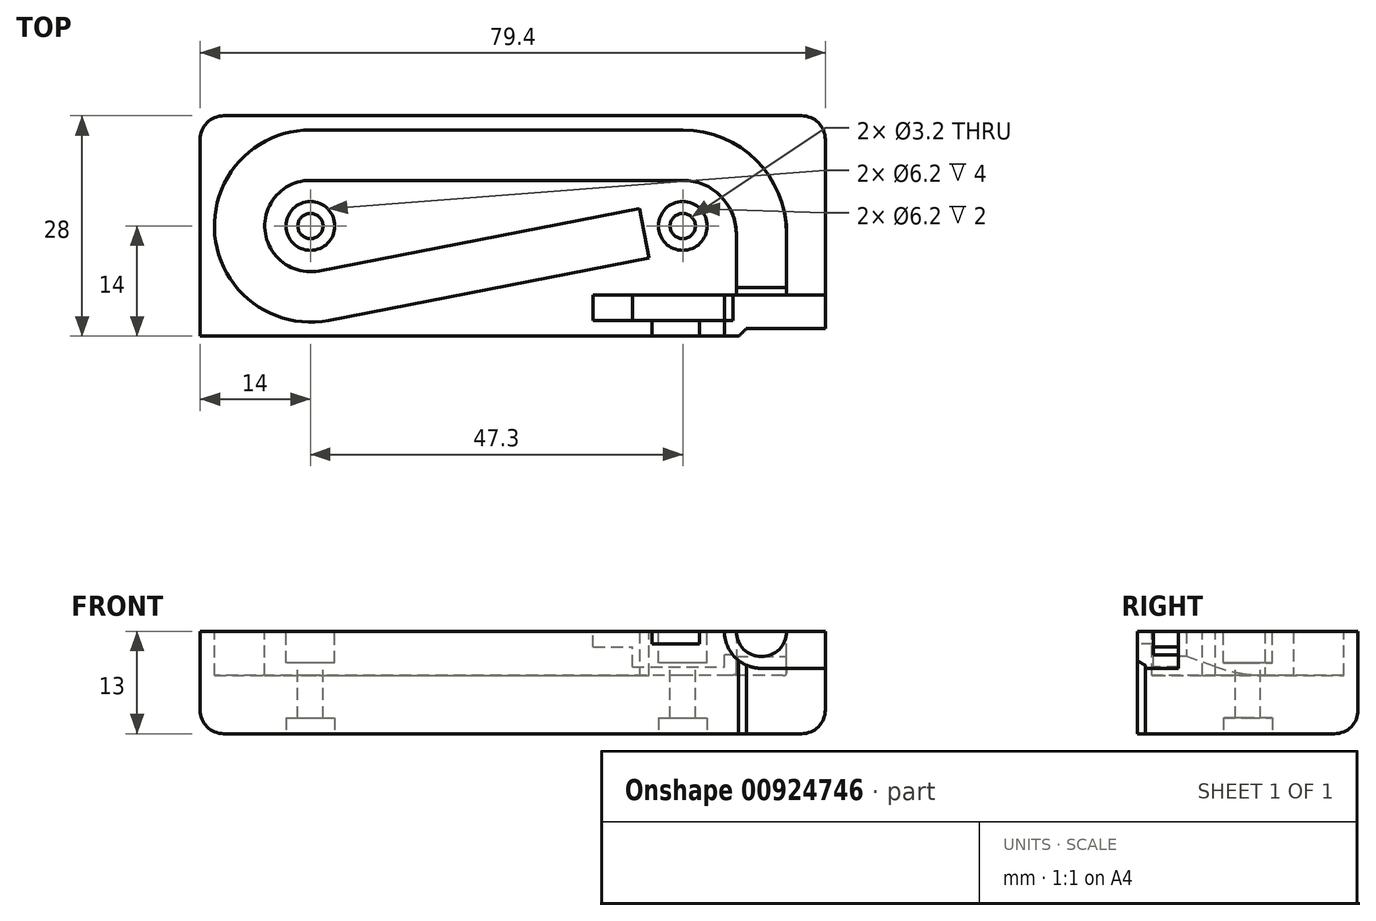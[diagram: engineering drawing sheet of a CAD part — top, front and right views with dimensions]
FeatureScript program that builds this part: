
annotation { "Feature Type Name" : "Feature", "Feature Type Description" : "" }
export const myFeature = defineFeature(function(context is Context, id is Id, definition is map)
    precondition{}
    {
        {
            var Q0;
            Q0=qCreatedBy(makeId("Top.planeOp"),FACE);
            var sketch = newSketch(context, id + "F0", { "sketchPlane" : qUnion([Q0])});
            skLineSegment(sketch, "E0.bottom", {"start": v(-71.3, -6.2) * mm, "end": v(8.1, -6.2) * mm});
            skLineSegment(sketch, "E0.top", {"start": v(-71.3, 21.8) * mm, "end": v(8.1, 21.8) * mm});
            skLineSegment(sketch, "E0.left", {"start": v(-71.3, -6.2) * mm, "end": v(-71.3, 21.8) * mm});
            skLineSegment(sketch, "E0.right", {"start": v(8.1, -6.2) * mm, "end": v(8.1, 21.8) * mm});
            skLineSegment(sketch, "E1", {"start": v(0, 0) * mm, "end": v(0, 6.8) * mm});
            skLineSegment(sketch, "E2", {"start": v(-10, 16.8) * mm, "end": v(-57.3, 16.8) * mm});
            skLineSegment(sketch, "E3", {"start": v(-55.59, -1.04) * mm, "end": v(-14.9, 6.85) * mm});
            skPoint(sketch, "E4.visualSharp", {"position": v(0, 16.8) * mm});
            skArc(sketch, "E4.filletArc", {"start": v(0, 6.8) * mm, "mid": v(-2.93, 13.87) * mm, "end": v(-10, 16.8) * mm});
            skLineSegment(sketch, "E5", {"start": v(0, 0) * mm, "end": v(0, -6.2) * mm});
            skCircle(sketch, "E6", {"center": v(-57.3, 7.8) * mm, "radius": 3.1 * mm});
            skPoint(sketch, "E6.centerSnap0", {"position": v(-71.3, 7.8) * mm});
            skCircle(sketch, "E7", {"center": v(-10, 7.8) * mm, "radius": 3.1 * mm});
            skPoint(sketch, "E7.centerSnap0", {"position": v(8.1, 7.8) * mm});
            skCircle(sketch, "E8", {"center": v(-57.3, 7.8) * mm, "radius": 1.6 * mm});
            skCircle(sketch, "E9", {"center": v(-10, 7.8) * mm, "radius": 1.6 * mm});
            skArc(sketch, "E10", {"start": v(-57.3, 16.8) * mm, "mid": v(-66.26, 6.94) * mm, "end": v(-55.59, -1.04) * mm});
            skLineSegment(sketch, "E11", {"start": v(8.1, -5.2) * mm, "end": v(-1.9, -5.2) * mm});
            skLineSegment(sketch, "E12", {"start": v(-1.9, -5.2) * mm, "end": v(-2.9, -6.2) * mm});
            skSolve(sketch);
        }
        {
            var Q0;
            Q0=makeQuery(id+"F0.imprint","IMPRINT",FACE,{"disambiguationData":[TD([[makeQuery(id+"F0.imprint","IMPRINT",EDGE,{"derivedFrom":sQuery(id+"F0.wireOp",EDGE,"7f5f69c7-28f1-4018-8948-6ec0e1df88dc.0")}),-1.0]])]});
            var Q1;
            {var subQ1=sQuery(id+"F0.wireOp",EDGE,"E0.top");Q1=makeQuery(id+"F0.imprint","IMPRINT",FACE,{"disambiguationData":[TD([[makeQuery(id+"F0.imprint","IMPRINT",EDGE,{"derivedFrom":subQ1}),-1.0]])]});}
            var Q2;
            Q2=makeQuery(id+"F0.imprint","IMPRINT",FACE,{"disambiguationData":[TD([[makeQuery(id+"F0.imprint","IMPRINT",EDGE,{"derivedFrom":sQuery(id+"F0.wireOp",EDGE,"E6")}),1.0]])]});
            var Q3;
            Q3=makeQuery(id+"F0.imprint","IMPRINT",FACE,{"disambiguationData":[TD([[makeQuery(id+"F0.imprint","IMPRINT",EDGE,{"derivedFrom":sQuery(id+"F0.wireOp",EDGE,"E7")}),1.0]])]});
            extrude(context, id + "F1", {"entities" : qUnion([Q0, Q1, Q2, Q3]), "oppositeDirection" : true, "depth" : 13 * mm, "offsetDistance" : 25 * mm});
        }
        {
            var Q0;
            Q0=makeQuery(id+"F0.imprint","IMPRINT",FACE,{"disambiguationData":[TD([[makeQuery(id+"F0.imprint","IMPRINT",EDGE,{"derivedFrom":sQuery(id+"F0.wireOp",EDGE,"E6")}),1.0]])]});
            var Q1;
            Q1=makeQuery(id+"F0.imprint","IMPRINT",FACE,{"disambiguationData":[TD([[makeQuery(id+"F0.imprint","IMPRINT",EDGE,{"derivedFrom":sQuery(id+"F0.wireOp",EDGE,"E7")}),1.0]])]});
            extrude(context, id + "F2", {"entities" : qUnion([Q0, Q1]), "operationType" : NewBodyOperationType.REMOVE, "oppositeDirection" : true, "depth" : 4 * mm, "offsetDistance" : 25 * mm});
        }
        {
            var Q0;
            Q0=makeQuery(id+"F1.opExtrude","CAP_FACE",FACE,{"disambiguationData":[OSD([sQuery(id+"F0.wireOp",EDGE,"E0.bottom"),sQuery(id+"F0.wireOp",EDGE,"E0.top"),sQuery(id+"F0.wireOp",EDGE,"E0.left"),sQuery(id+"F0.wireOp",EDGE,"E0.right"),sQuery(id+"F0.wireOp",EDGE,"E8"),sQuery(id+"F0.wireOp",EDGE,"E9")])],"isStart":false});
            var sketch = newSketch(context, id + "F3", { "sketchPlane" : qUnion([Q0])});
            skCircle(sketch, "E13.0", {"center": v(-10, -7.8) * mm, "radius": 3.1 * mm});
            skCircle(sketch, "E13.1", {"center": v(-57.3, -7.8) * mm, "radius": 3.1 * mm});
            skSolve(sketch);
        }
        {
            var Q0;
            Q0=qSketchRegion(id+"F3",true);
            extrude(context, id + "F4", {"entities" : qUnion([Q0]), "operationType" : NewBodyOperationType.REMOVE, "oppositeDirection" : true, "depth" : 2 * mm, "offsetDistance" : 25 * mm});
        }
        {
            var Q0;
            Q0=qCreatedBy(makeId("Front.planeOp"),FACE);
            var Q1;
            Q1=sQuery(id+"F0.wireOp",VERTEX,"E1.end");
            cPlane(context, id + "F5", {"entities" : qUnion([Q0, Q1]), "cplaneType" : CPlaneType.PLANE_POINT, "offset" : 25 * mm, "width" : 150 * mm, "height" : 150 * mm});
        }
        {
            var Q0;
            Q0=qCreatedBy(id+"F5.planeOp",FACE);
            var sketch = newSketch(context, id + "F6", { "sketchPlane" : qUnion([Q0])});
            skLineSegment(sketch, "E14", {"start": v(-3.2, 0) * mm, "end": v(3.2, 0) * mm});
            skLineSegment(sketch, "E15", {"start": v(3.2, 0) * mm, "end": v(3.2, -2.4) * mm});
            skLineSegment(sketch, "E16", {"start": v(-3.2, -2.4) * mm, "end": v(-3.2, 0) * mm});
            skArc(sketch, "E17", {"start": v(-3.2, -2.4) * mm, "mid": v(0, -5.6) * mm, "end": v(3.2, -2.4) * mm});
            skLineSegment(sketch, "E18", {"start": v(-3.2, -2.4) * mm, "end": v(-3.2, -5.6) * mm});
            skPoint(sketch, "E18.endSnap0", {"position": v(0, -5.6) * mm});
            skLineSegment(sketch, "E19", {"start": v(-3.2, -5.6) * mm, "end": v(3.2, -5.6) * mm});
            skLineSegment(sketch, "E20", {"start": v(3.2, -5.6) * mm, "end": v(3.2, -2.4) * mm});
            skSolve(sketch);
        }
        {
            var Q0;
            Q0=qCreatedBy(makeId("Right.planeOp"),FACE);
            var sketch = newSketch(context, id + "F7", { "sketchPlane" : qUnion([Q0])});
            skLineSegment(sketch, "E21", {"start": v(6.8, 0) * mm, "end": v(0, 2.4) * mm});
            skSolve(sketch);
        }
        {
            var Q0;
            Q0=qSketchRegion(id+"F6",true);
            var Q1;
            Q1=sQuery(id+"F0.wireOp",EDGE,"E4.filletArc");
            var Q2;
            Q2=sQuery(id+"F0.wireOp",EDGE,"E2");
            var Q3;
            Q3=sQuery(id+"F0.wireOp",EDGE,"d1730343-6995-424f-9b53-40ab9ed45578.filletArc");
            var Q4;
            Q4=sQuery(id+"F0.wireOp",EDGE,"4a9f4d60-a468-4d21-9085-bbe88fbe73fb.filletArc");
            var Q5;
            Q5=sQuery(id+"F0.wireOp",EDGE,"s2Idn5qi-RAJ9-igUd-Ia3V-9sphePnUOk5o");
            var Q6;
            Q6=sQuery(id+"F0.wireOp",EDGE,"E10");
            var Q7;
            Q7=sQuery(id+"F0.wireOp",EDGE,"E3");
            sweep(context, id + "F8", {"operationType" : NewBodyOperationType.REMOVE, "profiles" : qUnion([Q0]), "path" : qUnion([Q1, Q2, Q3, Q4, Q5, Q6, Q7])});
        }
        {
            var Q0;
            Q0=qSketchRegion(id+"F6",true);
            var Q1;
            Q1=sQuery(id+"F7.wireOp",EDGE,"E21");
            sweep(context, id + "F9", {"operationType" : NewBodyOperationType.REMOVE, "profiles" : qUnion([Q0]), "path" : qUnion([Q1])});
        }
        {
            var Q0;
            {var subQ0=sQuery(id+"F6.wireOp",EDGE,"E17");Q0=makeQuery(id+"F9.boolean.opBoolean","MERGE",EDGE,{"derivedFrom":[makeQuery(id+"F8.boolean.opBoolean","COPY",EDGE,{"derivedFrom":makeQuery(id+"F8.opSweep","CAP_EDGE",EDGE,{"disambiguationData":[OSD([sQuery(id+"F0.wireOp",VERTEX,"E4.filletArc.start"),subQ0])],"isStart":true})})],"fromTools":[makeQuery(id+"F9.opSweep","CAP_EDGE",EDGE,{"disambiguationData":[OSD([subQ0,sQuery(id+"F7.wireOp",VERTEX,"E21.start")])],"isStart":true})]});}
            fillet(context, id + "F10", {"entities" : qUnion([Q0]), "radius" : 20 * mm, "tangentPropagation" : true, "allowEdgeOverflow" : false});
        }
        {
            var Q0;
            Q0=makeQuery(id+"F1.opExtrude","SWEPT_FACE",FACE,{"disambiguationData":[OSD([sQuery(id+"F0.wireOp",EDGE,"E0.bottom")])]});
            var sketch = newSketch(context, id + "F11", { "sketchPlane" : qUnion([Q0])});
            skArc(sketch, "E22", {"start": v(-4.7, 0) * mm, "mid": v(-3.32, -3.32) * mm, "end": v(0, -4.7) * mm});
            skCircle(sketch, "E23", {"center": v(0, 0) * mm, "radius": 3.2 * mm});
            skLineSegment(sketch, "E24", {"start": v(0, -4.7) * mm, "end": v(8.1, -4.7) * mm});
            skLineSegment(sketch, "E25", {"start": v(8.1, -4.7) * mm, "end": v(8.1, 0) * mm});
            skLineSegment(sketch, "E26", {"start": v(8.1, 0) * mm, "end": v(-4.7, 0) * mm});
            skSolve(sketch);
        }
        {
            var Q0;
            Q0=qSketchRegion(id+"F11",true);
            extrude(context, id + "F12", {"entities" : qUnion([Q0]), "operationType" : NewBodyOperationType.REMOVE, "oppositeDirection" : true, "depth" : 5.2 * mm, "offsetDistance" : 25 * mm});
        }
        {
            var Q0;
            {var subQ0=sQuery(id+"F11.wireOp",EDGE,"E26");var subQ1=sQuery(id+"F11.wireOp",EDGE,"E23");var subQ2=makeQuery(id+"F11.imprint","INTERSECT",VERTEX,{"disambiguationData":[OD(0.0)],"derivedFrom":[subQ1,subQ0]});Q0=makeQuery(id+"F11.imprint","IMPRINT",FACE,{"disambiguationData":[TD([[makeQuery(id+"F11.imprint","IMPRINT",EDGE,{"disambiguationData":[TD([[subQ2,1.0]])],"derivedFrom":subQ1}),1.0]])]});}
            var Q1;
            {var subQ0=sQuery(id+"F11.wireOp",EDGE,"E26");var subQ1=sQuery(id+"F11.wireOp",EDGE,"E23");var subQ2=makeQuery(id+"F11.imprint","INTERSECT",VERTEX,{"disambiguationData":[OD(0.0)],"derivedFrom":[subQ1,subQ0]});Q1=makeQuery(id+"F11.imprint","IMPRINT",FACE,{"disambiguationData":[TD([[makeQuery(id+"F11.imprint","IMPRINT",EDGE,{"disambiguationData":[TD([[subQ2,-1.0]])],"derivedFrom":subQ1}),1.0]])]});}
            var Q2;
            {var subQ0=sQuery(id+"F11.wireOp",EDGE,"E26");var subQ1=sQuery(id+"F11.wireOp",EDGE,"E23");var subQ2=makeQuery(id+"F11.imprint","INTERSECT",VERTEX,{"disambiguationData":[OD(1.0)],"derivedFrom":[subQ1,subQ0]});Q2=makeQuery(id+"F11.imprint","IMPRINT",FACE,{"disambiguationData":[TD([[makeQuery(id+"F11.imprint","IMPRINT",EDGE,{"disambiguationData":[TD([[subQ2,1.0]])],"derivedFrom":subQ1}),1.0]])]});}
            var Q3;
            Q3=makeQuery(id+"F9.boolean.opBoolean","COPY",FACE,{"derivedFrom":makeQuery(id+"F9.opSweep","CAP_FACE",FACE,{"disambiguationData":[OSD([sQuery(id+"F6.wireOp",EDGE,"E14"),sQuery(id+"F6.wireOp",EDGE,"E15"),sQuery(id+"F6.wireOp",EDGE,"E16"),sQuery(id+"F6.wireOp",EDGE,"E17"),sQuery(id+"F7.wireOp",VERTEX,"E21.end")])],"isStart":false})});
            extrude(context, id + "F13", {"entities" : qUnion([Q0, Q1, Q2]), "operationType" : NewBodyOperationType.REMOVE, "endBound" : BoundingType.UP_TO_SURFACE, "oppositeDirection" : true, "depth" : 7 * mm, "endBoundEntityFace" : qUnion([Q3]), "offsetDistance" : 25 * mm});
        }
        {
            var Q0;
            Q0=qCreatedBy(makeId("Top.planeOp"),FACE);
            var sketch = newSketch(context, id + "F14", { "sketchPlane" : qUnion([Q0])});
            skLineSegment(sketch, "E27.bottom", {"start": v(-21.4, -1) * mm, "end": v(-4.7, -1) * mm});
            skLineSegment(sketch, "E27.top", {"start": v(-21.4, -4.2) * mm, "end": v(-4.7, -4.2) * mm});
            skLineSegment(sketch, "E27.left", {"start": v(-21.4, -1) * mm, "end": v(-21.4, -4.2) * mm});
            skLineSegment(sketch, "E27.right", {"start": v(-4.7, -1) * mm, "end": v(-4.7, -4.2) * mm});
            skLineSegment(sketch, "E28", {"start": v(-16.4, -1) * mm, "end": v(-16.4, -4.2) * mm});
            skLineSegment(sketch, "E29", {"start": v(-13.9, -4.2) * mm, "end": v(-13.9, -6.2) * mm});
            skLineSegment(sketch, "E30", {"start": v(-13.9, -6.2) * mm, "end": v(-7.9, -6.2) * mm});
            skLineSegment(sketch, "E31", {"start": v(-7.9, -6.2) * mm, "end": v(-7.9, -4.2) * mm});
            skLineSegment(sketch, "E32", {"start": v(-4.7, -4.2) * mm, "end": v(-2.7, -4.2) * mm});
            skLineSegment(sketch, "E33", {"start": v(-2.7, -4.2) * mm, "end": v(-2.7, -1) * mm});
            skLineSegment(sketch, "E34", {"start": v(-2.7, -1) * mm, "end": v(-4.7, -1) * mm});
            skSolve(sketch);
        }
        {
            var Q0;
            {var subQ0=sQuery(id+"F14.wireOp",EDGE,"E27.left");Q0=makeQuery(id+"F14.imprint","IMPRINT",FACE,{"disambiguationData":[TD([[makeQuery(id+"F14.imprint","IMPRINT",EDGE,{"derivedFrom":subQ0}),1.0]])]});}
            extrude(context, id + "F15", {"entities" : qUnion([Q0]), "operationType" : NewBodyOperationType.REMOVE, "oppositeDirection" : true, "depth" : 2 * mm, "offsetDistance" : 25 * mm});
        }
        {
            var Q0;
            {var subQ0=sQuery(id+"F14.wireOp",EDGE,"E27.right");Q0=makeQuery(id+"F14.imprint","IMPRINT",FACE,{"disambiguationData":[TD([[makeQuery(id+"F14.imprint","IMPRINT",EDGE,{"derivedFrom":subQ0}),-1.0]])]});}
            extrude(context, id + "F16", {"entities" : qUnion([Q0]), "operationType" : NewBodyOperationType.REMOVE, "oppositeDirection" : true, "depth" : 4.5 * mm, "offsetDistance" : 25 * mm});
        }
        {
            var Q0;
            {var subQ0=sQuery(id+"F14.wireOp",EDGE,"E29");Q0=makeQuery(id+"F14.imprint","IMPRINT",FACE,{"disambiguationData":[TD([[makeQuery(id+"F14.imprint","IMPRINT",EDGE,{"derivedFrom":subQ0}),1.0]])]});}
            extrude(context, id + "F17", {"entities" : qUnion([Q0]), "operationType" : NewBodyOperationType.REMOVE, "surfaceOperationType" : NewSurfaceOperationType.ADD, "oppositeDirection" : true, "depth" : 1.6 * mm, "offsetDistance" : 25 * mm});
        }
        {
            var Q0;
            Q0=makeQuery(id+"F14.imprint","IMPRINT",FACE,{"disambiguationData":[TD([[makeQuery(id+"F14.imprint","IMPRINT",EDGE,{"derivedFrom":sQuery(id+"F14.wireOp",EDGE,"E27.right")}),1.0]])]});
            extrude(context, id + "F18", {"entities" : qUnion([Q0]), "operationType" : NewBodyOperationType.REMOVE, "oppositeDirection" : true, "depth" : 3 * mm, "offsetDistance" : 25 * mm});
        }
        {
            var Q0;
            Q0=makeQuery(id+"F1.opExtrude","CAP_EDGE",EDGE,{"disambiguationData":[OSD([sQuery(id+"F0.wireOp",EDGE,"E0.right")])],"isStart":false});
            var Q1;
            Q1=makeQuery(id+"F1.opExtrude","CAP_EDGE",EDGE,{"disambiguationData":[OSD([sQuery(id+"F0.wireOp",EDGE,"E0.top")])],"isStart":false});
            var Q2;
            Q2=makeQuery(id+"F1.opExtrude","CAP_EDGE",EDGE,{"disambiguationData":[OSD([sQuery(id+"F0.wireOp",EDGE,"E0.left")])],"isStart":false});
            var Q3;
            Q3=makeQuery(id+"F1.opExtrude","SWEPT_EDGE",EDGE,{"disambiguationData":[OSD([sQuery(id+"F0.wireOp",EDGE,"E0.top"),sQuery(id+"F0.wireOp",EDGE,"E0.left")])]});
            var Q4;
            Q4=makeQuery(id+"F1.opExtrude","SWEPT_EDGE",EDGE,{"disambiguationData":[OSD([sQuery(id+"F0.wireOp",EDGE,"E0.top"),sQuery(id+"F0.wireOp",EDGE,"E0.right")])]});
            fillet(context, id + "F19", {"entities" : qUnion([Q0, Q1, Q2, Q3, Q4]), "radius" : 3 * mm, "tangentPropagation" : true, "allowEdgeOverflow" : false});
        }
    });
